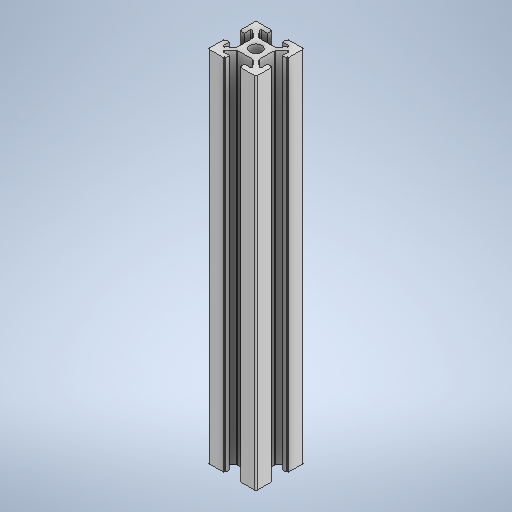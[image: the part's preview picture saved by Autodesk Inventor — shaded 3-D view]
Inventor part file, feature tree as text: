
AUTODESK INVENTOR PART (.ipt)
format: ipt  version: 2025.2 (Build 292293000, 293)  size: 376,832 bytes
history: native  units: mm
features: mirror x2, other x1, extrude x1, sketch x1
ambient origin geometry x8: Origin, YZ Plane, XZ Plane, XY Plane, X Axis, Y Axis, Z Axis, Center Point
bodies: Body1 (feature_tree)
feature tree (5):
  other  "Sólido1"
  extrude  "Extrusão1"  Depth=5.0mm
  mirror  "Espelhar1"
  mirror  "Espelhar2"
  sketch  "Esboço1"  dims[d0=20.0mm d2=5.0mm d4=2.0mm d5=0.5mm d6=0.174533mm d7=0.5mm d8=2.0mm d10=6.9mm d12=3.1mm d15=2.5mm d16=2.0mm d17=150.0mm d18=0.0mm d19=0.5mm d20=0.872665mm d21=0.5mm d22=0.872665mm]
